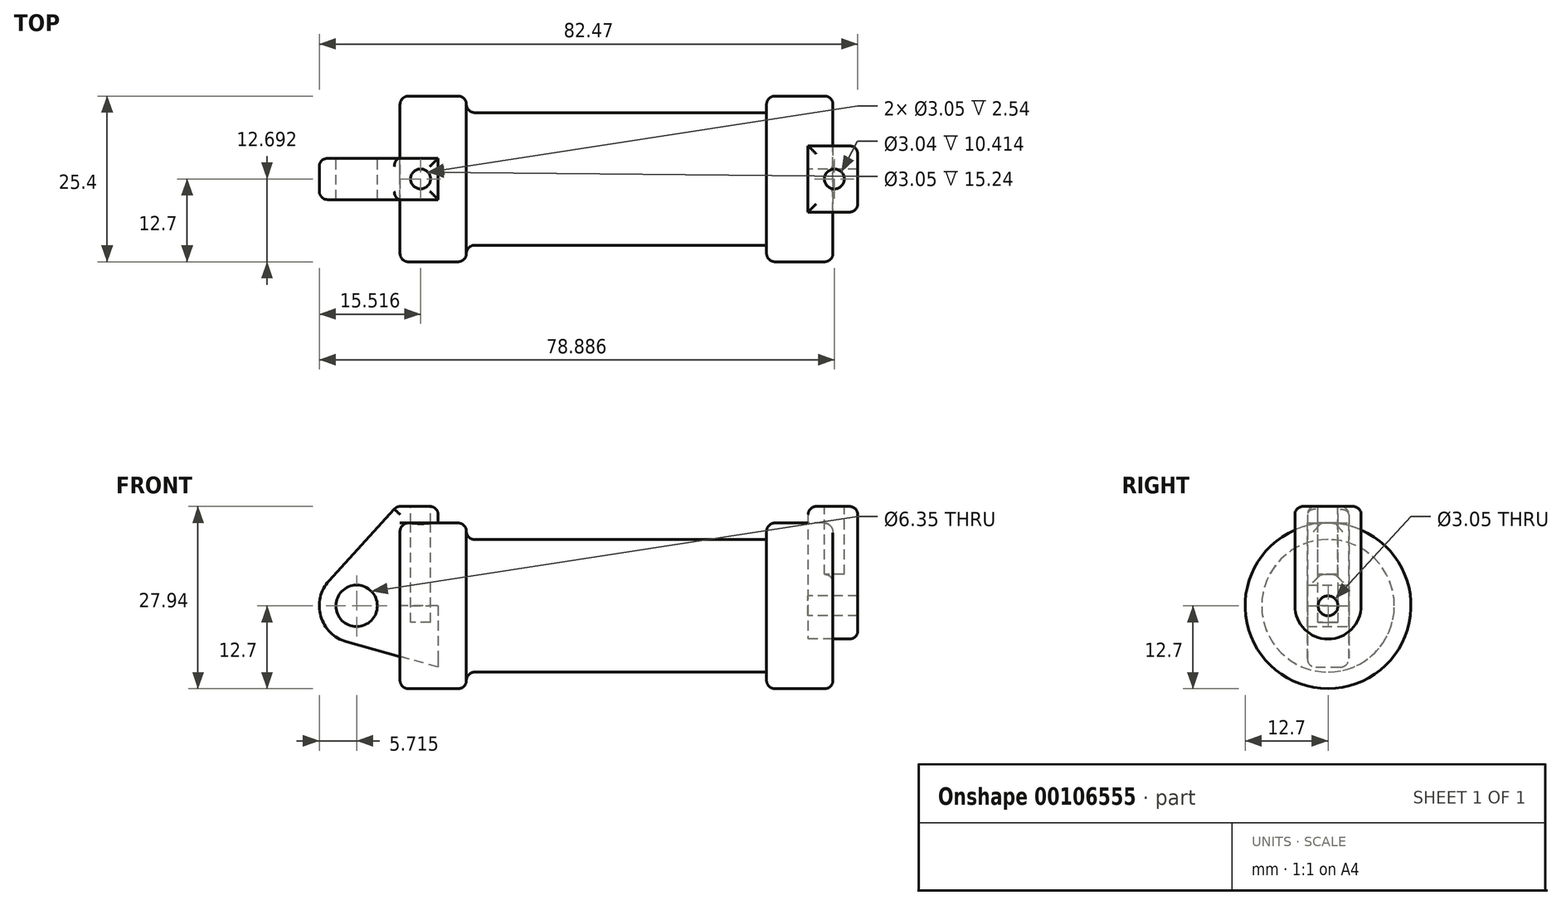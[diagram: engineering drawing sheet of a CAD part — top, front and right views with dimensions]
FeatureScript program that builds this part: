
annotation { "Feature Type Name" : "Feature", "Feature Type Description" : "" }
export const myFeature = defineFeature(function(context is Context, id is Id, definition is map)
    precondition{}
    {
        {
            var Q0;
            Q0=qCreatedBy(makeId("Front.planeOp"),FACE);
            var sketch = newSketch(context, id + "F0", { "sketchPlane" : qUnion([Q0])});
            skLineSegment(sketch, "E0", {"start": v(0, 0) * mm, "end": v(0, 12.7) * mm});
            skLineSegment(sketch, "E1", {"start": v(0, 12.7) * mm, "end": v(10.16, 12.7) * mm});
            skLineSegment(sketch, "E2", {"start": v(10.16, 12.7) * mm, "end": v(10.16, 10.16) * mm});
            skLineSegment(sketch, "E3", {"start": v(10.16, 10.16) * mm, "end": v(56.13, 10.16) * mm});
            skLineSegment(sketch, "E4", {"start": v(56.13, 10.16) * mm, "end": v(56.13, 12.7) * mm});
            skLineSegment(sketch, "E5", {"start": v(56.13, 12.7) * mm, "end": v(66.3, 12.7) * mm});
            skLineSegment(sketch, "E6", {"start": v(66.3, 12.7) * mm, "end": v(66.3, 0) * mm});
            skLineSegment(sketch, "E7", {"start": v(66.3, 0) * mm, "end": v(0, 0) * mm});
            skLineSegment(sketch, "E8", {"start": v(5.84, 15.24) * mm, "end": v(-0.5, 15.24) * mm});
            skLineSegment(sketch, "E9", {"start": v(-0.5, 15.24) * mm, "end": v(-10.88, 3.85) * mm});
            skLineSegment(sketch, "E10", {"start": v(0, 0) * mm, "end": v(-6.65, 0) * mm});
            skCircle(sketch, "E11", {"center": v(-6.65, 0) * mm, "radius": 5.72 * mm});
            skCircle(sketch, "E12", {"center": v(-6.65, 0) * mm, "radius": 3.18 * mm});
            skLineSegment(sketch, "E13", {"start": v(5.84, 15.24) * mm, "end": v(5.84, -9.4) * mm});
            skLineSegment(sketch, "E14", {"start": v(5.84, -9.4) * mm, "end": v(-8.18, -5.5) * mm});
            skSolve(sketch);
        }
        {
            var Q0;
            {var subQ0=sQuery(id+"F0.wireOp",EDGE,"E0");Q0=makeQuery(id+"F0.imprint","IMPRINT",FACE,{"disambiguationData":[TD([[makeQuery(id+"F0.imprint","IMPRINT",EDGE,{"derivedFrom":subQ0}),-1.0]])]});}
            var Q1;
            {var subQ0=sQuery(id+"F0.wireOp",EDGE,"E2");Q1=makeQuery(id+"F0.imprint","IMPRINT",FACE,{"disambiguationData":[TD([[makeQuery(id+"F0.imprint","IMPRINT",EDGE,{"derivedFrom":subQ0}),-1.0]])]});}
            var Q2;
            Q2=sQuery(id+"F0.wireOp",EDGE,"E7");
            revolve(context, id + "F1", {"entities" : qUnion([Q0, Q1]), "axis" : qUnion([Q2]), "revolveType" : RevolveType.FULL, "oppositeDirection" : true});
        }
        {
            var Q0;
            Q0=makeQuery(id+"F1.opRevolve","SWEPT_FACE",FACE,{"disambiguationData":[OSD([sQuery(id+"F0.wireOp",EDGE,"E6")])]});
            var sketch = newSketch(context, id + "F2", { "sketchPlane" : qUnion([Q0])});
            skCircle(sketch, "E15", {"center": v(0, 0) * mm, "radius": 1.52 * mm});
            skCircle(sketch, "E16", {"center": v(0, 0) * mm, "radius": 5.08 * mm});
            skLineSegment(sketch, "E17", {"start": v(-5.08, 0) * mm, "end": v(-5.08, 15.24) * mm});
            skLineSegment(sketch, "E18", {"start": v(-5.08, 15.24) * mm, "end": v(5.08, 15.24) * mm});
            skLineSegment(sketch, "E19", {"start": v(5.08, 15.24) * mm, "end": v(5.08, 0) * mm});
            skSolve(sketch);
        }
        {
            var Q0;
            {var subQ3=sQuery(id+"F0.wireOp",EDGE,"E0");Q0=makeQuery(id+"F0.imprint","IMPRINT",FACE,{"disambiguationData":[TD([[makeQuery(id+"F0.imprint","IMPRINT",EDGE,{"derivedFrom":subQ3}),1.0]])]});}
            var Q1;
            {var subQ0=sQuery(id+"F0.wireOp",EDGE,"E14");Q1=makeQuery(id+"F0.imprint","IMPRINT",FACE,{"disambiguationData":[TD([[makeQuery(id+"F0.imprint","IMPRINT",EDGE,{"derivedFrom":subQ0}),-1.0]])]});}
            var Q2;
            {var subQ4=sQuery(id+"F0.wireOp",EDGE,"E12");Q2=makeQuery(id+"F0.imprint","IMPRINT",FACE,{"disambiguationData":[TD([[makeQuery(id+"F0.imprint","IMPRINT",EDGE,{"derivedFrom":subQ4}),-1.0]])]});}
            extrude(context, id + "F3", {"entities" : qUnion([Q0, Q1, Q2]), "endBound" : BoundingType.SYMMETRIC, "depth" : 6.35 * mm});
        }
        {
            var Q0;
            Q0=makeQuery(id+"F2.imprint","IMPRINT",FACE,{"disambiguationData":[TD([[makeQuery(id+"F2.imprint","IMPRINT",EDGE,{"derivedFrom":sQuery(id+"F2.wireOp",EDGE,"E15")}),-1.0]])]});
            var Q1;
            {var subQ0=sQuery(id+"F2.wireOp",EDGE,"E17");var subQ1=sQuery(id+"F2.wireOp",EDGE,"E16");var subQ2=makeQuery(id+"F2.imprint","INTERSECT",VERTEX,{"derivedFrom":[subQ1,subQ0]});Q1=makeQuery(id+"F2.imprint","IMPRINT",FACE,{"disambiguationData":[TD([[makeQuery(id+"F2.imprint","IMPRINT",EDGE,{"disambiguationData":[TD([[subQ2,1.0]])],"derivedFrom":subQ1}),-1.0]])]});}
            var Q2;
            {var subQ0=sQuery(id+"F2.wireOp",EDGE,"E18");Q2=makeQuery(id+"F2.imprint","IMPRINT",FACE,{"disambiguationData":[TD([[makeQuery(id+"F2.imprint","IMPRINT",EDGE,{"derivedFrom":subQ0}),-1.0]])]});}
            extrude(context, id + "F4", {"entities" : qUnion([Q0, Q1, Q2]), "endBound" : BoundingType.SYMMETRIC, "depth" : 7.62 * mm});
        }
        {
            var Q0;
            Q0=makeQuery(id+"F4.opExtrude","SWEPT_FACE",FACE,{"disambiguationData":[OSD([sQuery(id+"F2.wireOp",EDGE,"E18")])]});
            var sketch = newSketch(context, id + "F5", { "sketchPlane" : qUnion([Q0])});
            skCircle(sketch, "E20", {"center": v(66.52, 0) * mm, "radius": 1.52 * mm});
            skSolve(sketch);
        }
        {
            var Q0;
            Q0=makeQuery(id+"F5.imprint","IMPRINT",FACE,{"disambiguationData":[TD([[makeQuery(id+"F5.imprint","IMPRINT",EDGE,{"derivedFrom":sQuery(id+"F5.wireOp",EDGE,"E20")}),1.0]])]});
            var Q1;
            Q1=sQuery(id+"F5.wireOp",EDGE,"E20");
            extrude(context, id + "F6", {"entities" : qUnion([Q0]), "operationType" : NewBodyOperationType.REMOVE, "surfaceEntities" : qUnion([Q1]), "oppositeDirection" : true, "depth" : 10.4 * mm});
        }
        {
            var Q0;
            Q0=makeQuery(id+"F3.opExtrude","SWEPT_FACE",FACE,{"disambiguationData":[OSD([sQuery(id+"F0.wireOp",EDGE,"E8")])]});
            var sketch = newSketch(context, id + "F7", { "sketchPlane" : qUnion([Q0])});
            skCircle(sketch, "E21", {"center": v(3.15, 0) * mm, "radius": 1.52 * mm});
            skPoint(sketch, "E21.centerSnap0", {"position": v(-0.5, 0) * mm});
            skSolve(sketch);
        }
        {
            var Q0;
            Q0 = qSketchRegion(id + "F7", true);
            extrude(context, id + "F8", {"entities" : qUnion([Q0]), "operationType" : NewBodyOperationType.REMOVE, "oppositeDirection" : true, "depth" : 17.78 * mm});
        }
        {
            var Q0;
            Q0=makeQuery(id+"F1.opRevolve","SWEPT_EDGE",EDGE,{"disambiguationData":[OSD([sQuery(id+"F0.wireOp",EDGE,"E2"),sQuery(id+"F0.wireOp",EDGE,"E3")])]});
            var Q1;
            Q1=makeQuery(id+"F1.opRevolve","SWEPT_EDGE",EDGE,{"disambiguationData":[OSD([sQuery(id+"F0.wireOp",EDGE,"E4"),sQuery(id+"F0.wireOp",EDGE,"E5")])]});
            fillet(context, id + "F9", {"entities" : qUnion([Q0, Q1]), "radius" : 1.27 * mm, "tangentPropagation" : true, "allowEdgeOverflow" : false});
        }
        {
            var Q0;
            Q0=makeQuery(id+"F1.opRevolve","SWEPT_EDGE",EDGE,{"disambiguationData":[OSD([sQuery(id+"F0.wireOp",EDGE,"E0"),sQuery(id+"F0.wireOp",EDGE,"E1")])]});
            var Q1;
            Q1=makeQuery(id+"F3.opExtrude","CAP_EDGE",EDGE,{"disambiguationData":[OSD([sQuery(id+"F0.wireOp",EDGE,"E11")])],"isStart":true});
            var Q2;
            Q2=makeQuery(id+"F3.opExtrude","CAP_EDGE",EDGE,{"disambiguationData":[OSD([sQuery(id+"F0.wireOp",EDGE,"E14")])],"isStart":true});
            var Q3;
            Q3=makeQuery(id+"F3.opExtrude","CAP_EDGE",EDGE,{"disambiguationData":[OSD([sQuery(id+"F0.wireOp",EDGE,"E14")])],"isStart":false});
            var Q4;
            Q4=makeQuery(id+"F3.opExtrude","CAP_EDGE",EDGE,{"disambiguationData":[OSD([sQuery(id+"F0.wireOp",EDGE,"E11")])],"isStart":false});
            var Q5;
            Q5=makeQuery(id+"F3.opExtrude","CAP_EDGE",EDGE,{"disambiguationData":[OSD([sQuery(id+"F0.wireOp",EDGE,"E9")])],"isStart":false});
            var Q6;
            Q6=makeQuery(id+"F3.opExtrude","CAP_EDGE",EDGE,{"disambiguationData":[OSD([sQuery(id+"F0.wireOp",EDGE,"E9")])],"isStart":true});
            fillet(context, id + "F10", {"entities" : qUnion([Q0, Q1, Q2, Q3, Q4, Q5, Q6]), "radius" : 1.27 * mm, "tangentPropagation" : true, "allowEdgeOverflow" : false});
        }
        {
            var Q0;
            Q0=makeQuery(id+"F1.opRevolve","SWEPT_EDGE",EDGE,{"disambiguationData":[OSD([sQuery(id+"F0.wireOp",EDGE,"E5"),sQuery(id+"F0.wireOp",EDGE,"E6")])]});
            var Q1;
            Q1=makeQuery(id+"F4.opExtrude","CAP_EDGE",EDGE,{"disambiguationData":[OSD([sQuery(id+"F2.wireOp",EDGE,"E17")])],"isStart":false});
            var Q2;
            Q2=makeQuery(id+"F1.opRevolve","SWEPT_FACE",FACE,{"disambiguationData":[OSD([sQuery(id+"F0.wireOp",EDGE,"E6")])]});
            fillet(context, id + "F11", {"entities" : qUnion([Q0, Q1, Q2]), "radius" : 1.27 * mm, "tangentPropagation" : true, "allowEdgeOverflow" : false});
        }
        {
            var Q0;
            Q0=makeQuery(id+"F4.opExtrude","SWEPT_EDGE",EDGE,{"disambiguationData":[OSD([sQuery(id+"F2.wireOp",EDGE,"E18"),sQuery(id+"F2.wireOp",EDGE,"E19")])]});
            var Q1;
            Q1=makeQuery(id+"F4.opExtrude","CAP_EDGE",EDGE,{"disambiguationData":[OSD([sQuery(id+"F2.wireOp",EDGE,"E18")])],"isStart":false});
            var Q2;
            Q2=makeQuery(id+"F4.opExtrude","CAP_EDGE",EDGE,{"disambiguationData":[OSD([sQuery(id+"F2.wireOp",EDGE,"E18")])],"isStart":true});
            var Q3;
            Q3=makeQuery(id+"F4.opExtrude","SWEPT_EDGE",EDGE,{"disambiguationData":[OSD([sQuery(id+"F2.wireOp",EDGE,"E17"),sQuery(id+"F2.wireOp",EDGE,"E18")])]});
            var Q4;
            Q4=makeQuery(id+"F3.opExtrude","CAP_EDGE",EDGE,{"disambiguationData":[OSD([sQuery(id+"F0.wireOp",EDGE,"E8")])],"isStart":false});
            var Q5;
            Q5=makeQuery(id+"F3.opExtrude","SWEPT_EDGE",EDGE,{"disambiguationData":[OSD([sQuery(id+"F0.wireOp",EDGE,"E8"),sQuery(id+"F0.wireOp",EDGE,"E13")])]});
            var Q6;
            Q6=makeQuery(id+"F3.opExtrude","CAP_EDGE",EDGE,{"disambiguationData":[OSD([sQuery(id+"F0.wireOp",EDGE,"E8")])],"isStart":true});
            var Q7;
            Q7=makeQuery(id+"F3.opExtrude","SWEPT_EDGE",EDGE,{"disambiguationData":[OSD([sQuery(id+"F0.wireOp",EDGE,"E8"),sQuery(id+"F0.wireOp",EDGE,"E9")])]});
            fillet(context, id + "F12", {"entities" : qUnion([Q0, Q1, Q2, Q3, Q4, Q5, Q6, Q7]), "radius" : 1.27 * mm, "tangentPropagation" : true, "allowEdgeOverflow" : false});
        }
        {
            var Q0;
            Q0=makeQuery(id+"F1.opRevolve","SWEPT_EDGE",EDGE,{"disambiguationData":[OSD([sQuery(id+"F0.wireOp",EDGE,"E1"),sQuery(id+"F0.wireOp",EDGE,"E2")])]});
            var Q1;
            {var subQ0=sQuery(id+"F0.wireOp",EDGE,"E5");Q1=makeQuery(id+"F11.opFillet","BLEND_EDGE",EDGE,{"blendedFrom":[makeQuery(id+"F1.opRevolve","SWEPT_EDGE",EDGE,{"disambiguationData":[OSD([subQ0,sQuery(id+"F0.wireOp",EDGE,"E6")])]}),makeQuery(id+"F1.opRevolve","SWEPT_FACE",FACE,{"disambiguationData":[OSD([subQ0])]})],"blendedInto":[makeQuery(id+"F1.opRevolve","SWEPT_FACE",FACE,{"disambiguationData":[OSD([subQ0])]})]});}
            fillet(context, id + "F13", {"entities" : qUnion([Q0, Q1]), "radius" : 1.27 * mm, "tangentPropagation" : true, "allowEdgeOverflow" : false});
        }
    });
